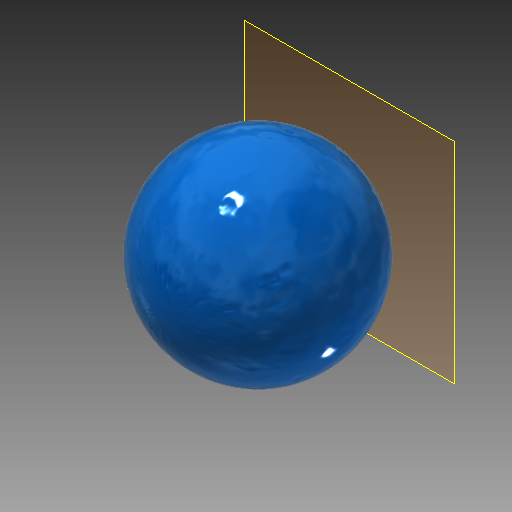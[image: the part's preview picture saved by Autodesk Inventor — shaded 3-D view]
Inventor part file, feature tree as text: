
AUTODESK INVENTOR PART (.ipt)
format: ipt  version: 2019 (Build 230136000, 136)  size: 215,040 bytes
history: native  units: mm
features: other x4, extrude x2, thread x1, sketch x1, projected_geometry x1
ambient origin geometry x8: Origin, YZ Plane, XZ Plane, XY Plane, X Axis, Y Axis, Z Axis, Center Point
bodies: Solid1 (feature_tree)
feature tree (9):
  other  "Ball"
  other  "BottomCuttingPlane"
  extrude  "FlattenBottom"  Depth=10.0mm
  extrude  "Extrusion2"  TaperAngle=90.0deg  [1 undecoded]
  thread  "Thread1"  [1 undecoded]
  sketch  "Sketch1"  dims[d0=36.0mm d1=36.0mm d2=90.0deg d3=-17.25mm d4=10.0mm d5=0.0mm d6=8.0mm d7=5.0mm d8=10.0mm d9=0.0mm d10=10.0mm d11=0.0mm]
  other  "CutBottomSketch"
  other  "Anchor"
  projected_geometry  "Project Cut Edges1"
note: 2 required parameter values undecoded (feature->parameter linkage not recoverable at this tier; creation-order binding heuristic only, values carry confidence <= 0.55)
